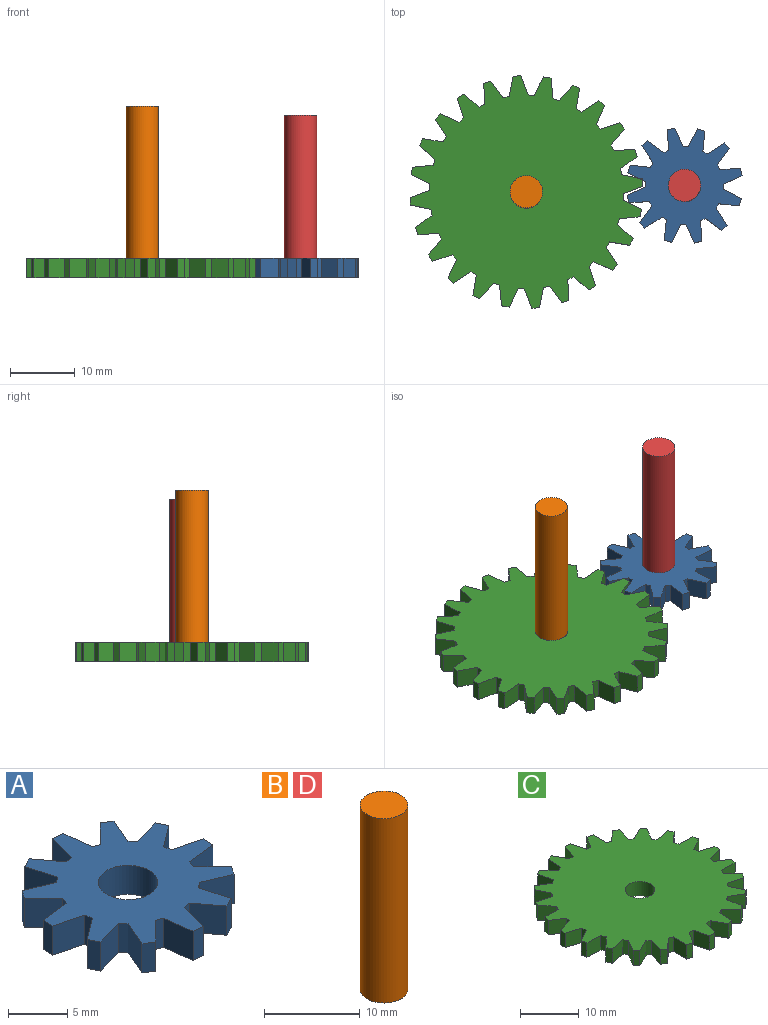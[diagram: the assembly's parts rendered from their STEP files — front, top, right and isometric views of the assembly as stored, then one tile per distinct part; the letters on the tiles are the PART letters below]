
ASSEMBLY  parts=4 mates=2
PART A: 51 faces, bbox 18x18x3 mm
  f0: plane 3x1.17mm, normal (-1,0.07,0), area 3.5mm2, adj f1,f48,f49,f50
  f1: plane 3.05x3mm, normal (-0.25,-0.97,0), area 9.5mm2, adj f0,f2,f49,f50
  f2: plane 3x0.77mm, normal (-0.98,-0.2,0), area 2.4mm2, adj f1,f3,f49,f50
  f3: plane 3x2.52mm, normal (-0.6,0.8,0), area 9.5mm2, adj f2,f4,f49,f50
  f4: plane 3x1.06mm, normal (-0.9,-0.44,0), area 3.5mm2, adj f3,f5,f49,f50
  f5: plane 3.03x3mm, normal (0.27,-0.96,0), area 9.5mm2, adj f4,f6,f49,f50
  f6: plane 3x0.59mm, normal (-0.75,-0.66,0), area 2.4mm2, adj f5,f7,f49,f50
  f7: plane 3x2.9mm, normal (-0.92,0.39,0), area 9.5mm2, adj f6,f8,f49,f50
  f8: plane 3x0.98mm, normal (-0.56,-0.83,0), area 3.5mm2, adj f7,f9,f49,f50
  f9: plane 3x2.25mm, normal (0.71,-0.7,0), area 9.5mm2, adj f8,f10,f49,f50
  f10: plane 3x0.74mm, normal (-0.32,-0.95,0), area 2.4mm2, adj f9,f11,f49,f50
  f11: plane 3.13x3mm, normal (-0.99,-0.12,0), area 9.5mm2, adj f10,f12,f49,f50
  f12: plane 3x1.17mm, normal (-0.07,-1,0), area 3.5mm2, adj f11,f13,f49,f50
  f13: plane 3.05x3mm, normal (0.97,-0.25,0), area 9.5mm2, adj f12,f14,f49,f50
  f14: plane 3x0.77mm, normal (0.2,-0.98,0), area 2.4mm2, adj f13,f15,f49,f50
  f15: plane 3x2.52mm, normal (-0.8,-0.6,0), area 9.5mm2, adj f14,f16,f49,f50
  f16: plane 3x1.06mm, normal (0.44,-0.9,0), area 3.5mm2, adj f15,f17,f49,f50
  f17: plane 3.03x3mm, normal (0.96,0.27,0), area 9.5mm2, adj f16,f18,f49,f50
  f18: plane 3x0.59mm, normal (0.66,-0.75,0), area 2.4mm2, adj f17,f19,f49,f50
  f19: plane 3x2.9mm, normal (-0.39,-0.92,0), area 9.5mm2, adj f18,f20,f49,f50
  f20: plane 3x0.98mm, normal (0.83,-0.56,0), area 3.5mm2, adj f19,f21,f49,f50
  f21: plane 3x2.25mm, normal (0.7,0.71,0), area 9.5mm2, adj f20,f22,f49,f50
  f22: plane 3x0.74mm, normal (0.95,-0.32,0), area 2.4mm2, adj f21,f23,f49,f50
  f23: plane 3.13x3mm, normal (0.12,-0.99,0), area 9.5mm2, adj f22,f24,f49,f50
  f24: plane 3x1.17mm, normal (1,-0.07,0), area 3.5mm2, adj f23,f25,f49,f50
  f25: plane 3.05x3mm, normal (0.25,0.97,0), area 9.5mm2, adj f24,f26,f49,f50
  f26: plane 3x0.77mm, normal (0.98,0.2,0), area 2.4mm2, adj f25,f27,f49,f50
  f27: plane 3x2.52mm, normal (0.6,-0.8,0), area 9.5mm2, adj f26,f28,f49,f50
  f28: plane 3x1.06mm, normal (0.9,0.44,0), area 3.5mm2, adj f27,f29,f49,f50
  f29: plane 3.03x3mm, normal (-0.27,0.96,0), area 9.5mm2, adj f28,f30,f49,f50
  f30: plane 3x0.59mm, normal (0.75,0.66,0), area 2.4mm2, adj f29,f31,f49,f50
  f31: plane 3x2.9mm, normal (0.92,-0.39,0), area 9.5mm2, adj f30,f32,f49,f50
  f32: plane 3x0.98mm, normal (0.56,0.83,0), area 3.5mm2, adj f31,f33,f49,f50
  f33: plane 3x2.25mm, normal (-0.71,0.7,0), area 9.5mm2, adj f32,f34,f49,f50
  f34: plane 3x0.74mm, normal (0.32,0.95,0), area 2.4mm2, adj f33,f35,f49,f50
  f35: plane 3.13x3mm, normal (0.99,0.12,0), area 9.5mm2, adj f34,f36,f49,f50
  f36: plane 3x1.17mm, normal (0.07,1,0), area 3.5mm2, adj f35,f37,f49,f50
  f37: plane 3.05x3mm, normal (-0.97,0.25,0), area 9.5mm2, adj f36,f38,f49,f50
  f38: plane 3x0.77mm, normal (-0.2,0.98,0), area 2.4mm2, adj f37,f39,f49,f50
  f39: plane 3x2.52mm, normal (0.8,0.6,0), area 9.5mm2, adj f38,f40,f49,f50
  f40: plane 3x1.06mm, normal (-0.44,0.9,0), area 3.5mm2, adj f39,f41,f49,f50
  f41: plane 3.03x3mm, normal (-0.96,-0.27,0), area 9.5mm2, adj f40,f42,f49,f50
  f42: plane 3x0.59mm, normal (-0.66,0.75,0), area 2.4mm2, adj f41,f43,f49,f50
  f43: plane 3x2.9mm, normal (0.39,0.92,0), area 9.5mm2, adj f42,f44,f49,f50
  f44: plane 3x0.98mm, normal (-0.83,0.56,0), area 3.5mm2, adj f43,f45,f49,f50
  f45: plane 3x2.25mm, normal (-0.7,-0.71,0), area 9.5mm2, adj f44,f46,f49,f50
  f46: plane 3x0.74mm, normal (-0.95,0.32,0), area 2.4mm2, adj f45,f48,f49,f50
  f47: cylinder r=2.5mm len=5mm, axis (0,0,-1), area 47.1mm2, adj f49,f50
  f48: plane 3.13x3mm, normal (-0.12,0.99,0), area 9.5mm2, adj f0,f46,f49,f50
  f49: plane 18x18mm, normal (0,0,1), area 156.6mm2, adj f0,f1,f2,f3,f4,f5,f6,f7
  f50: plane 18x18mm, normal (0,0,-1), area 156.6mm2, adj f0,f1,f2,f3,f4,f5,f6,f7
PART B: 3 faces, bbox 5x5x23.5 mm
  f0: cylinder r=2.5mm len=23.54mm, axis (0,0,-1), area 369.8mm2, adj f1,f2
  f1: plane 5x5mm, normal (0,0,1), area 19.6mm2, adj f0
  f2: plane 5x5mm, normal (0,0,-1), area 19.6mm2, adj f0
PART C: 99 faces, bbox 36x36x3 mm
  f0: plane 3x1.18mm, normal (-1,0.03,0), area 3.5mm2, adj f1,f96,f97,f98
  f1: plane 3.03x3mm, normal (-0.31,-0.95,0), area 9.6mm2, adj f0,f2,f97,f98
  f2: plane 3x0.98mm, normal (-1,-0.1,0), area 2.9mm2, adj f1,f3,f97,f98
  f3: plane 3x2.78mm, normal (-0.49,0.87,0), area 9.6mm2, adj f2,f4,f97,f98
  f4: plane 3x1.15mm, normal (-0.97,-0.23,0), area 3.5mm2, adj f3,f5,f97,f98
  f5: plane 3.18x3mm, normal (-0.05,-1,0), area 9.6mm2, adj f4,f6,f97,f98
  f6: plane 3x0.92mm, normal (-0.94,-0.35,0), area 2.9mm2, adj f5,f7,f97,f98
  f7: plane 3x2.29mm, normal (-0.7,0.72,0), area 9.6mm2, adj f6,f8,f97,f98
  f8: plane 3x1.04mm, normal (-0.88,-0.47,0), area 3.5mm2, adj f7,f9,f97,f98
  f9: plane 3.12x3mm, normal (0.21,-0.98,0), area 9.6mm2, adj f8,f10,f97,f98
  f10: plane 3x0.8mm, normal (-0.81,-0.58,0), area 2.9mm2, adj f9,f11,f97,f98
  f11: plane 3x2.74mm, normal (-0.86,0.51,0), area 9.6mm2, adj f10,f12,f97,f98
  f12: plane 3x0.86mm, normal (-0.73,-0.68,0), area 3.5mm2, adj f11,f13,f97,f98
  f13: plane 3x2.84mm, normal (0.46,-0.89,0), area 9.6mm2, adj f12,f14,f97,f98
  f14: plane 3x0.76mm, normal (-0.63,-0.77,0), area 2.9mm2, adj f13,f15,f97,f98
  f15: plane 3.07x3mm, normal (-0.96,0.27,0), area 9.6mm2, adj f14,f16,f97,f98
  f16: plane 3x1mm, normal (-0.53,-0.85,0), area 3.5mm2, adj f15,f17,f97,f98
  f17: plane 3x2.37mm, normal (0.67,-0.74,0), area 9.6mm2, adj f16,f18,f97,f98
  f18: plane 3x0.89mm, normal (-0.41,-0.91,0), area 2.9mm2, adj f17,f19,f97,f98
  f19: plane 3.19x3mm, normal (-1,0.01,0), area 9.6mm2, adj f18,f20,f97,f98
  f20: plane 3x1.13mm, normal (-0.29,-0.96,0), area 3.5mm2, adj f19,f21,f97,f98
  f21: plane 3x2.68mm, normal (0.84,-0.54,0), area 9.6mm2, adj f20,f22,f97,f98
  f22: plane 3x0.97mm, normal (-0.16,-0.99,0), area 2.9mm2, adj f21,f23,f97,f98
  f23: plane 3.09x3mm, normal (-0.97,-0.24,0), area 9.6mm2, adj f22,f24,f97,f98
  f24: plane 3x1.18mm, normal (-0.03,-1,0), area 3.5mm2, adj f23,f25,f97,f98
  f25: plane 3.03x3mm, normal (0.95,-0.31,0), area 9.6mm2, adj f24,f26,f97,f98
  f26: plane 3x0.98mm, normal (0.1,-1,0), area 2.9mm2, adj f25,f27,f97,f98
  f27: plane 3x2.78mm, normal (-0.87,-0.49,0), area 9.6mm2, adj f26,f28,f97,f98
  f28: plane 3x1.15mm, normal (0.23,-0.97,0), area 3.5mm2, adj f27,f29,f97,f98
  f29: plane 3.18x3mm, normal (1,-0.05,0), area 9.6mm2, adj f28,f30,f97,f98
  f30: plane 3x0.92mm, normal (0.35,-0.94,0), area 2.9mm2, adj f29,f31,f97,f98
  f31: plane 3x2.29mm, normal (-0.72,-0.7,0), area 9.6mm2, adj f30,f32,f97,f98
  f32: plane 3x1.04mm, normal (0.47,-0.88,0), area 3.5mm2, adj f31,f33,f97,f98
  f33: plane 3.12x3mm, normal (0.98,0.21,0), area 9.6mm2, adj f32,f34,f97,f98
  f34: plane 3x0.8mm, normal (0.58,-0.81,0), area 2.9mm2, adj f33,f35,f97,f98
  f35: plane 3x2.74mm, normal (-0.51,-0.86,0), area 9.6mm2, adj f34,f36,f97,f98
  f36: plane 3x0.86mm, normal (0.68,-0.73,0), area 3.5mm2, adj f35,f37,f97,f98
  f37: plane 3x2.84mm, normal (0.89,0.46,0), area 9.6mm2, adj f36,f38,f97,f98
  f38: plane 3x0.76mm, normal (0.77,-0.63,0), area 2.9mm2, adj f37,f39,f97,f98
  f39: plane 3.07x3mm, normal (-0.27,-0.96,0), area 9.6mm2, adj f38,f40,f97,f98
  f40: plane 3x1mm, normal (0.85,-0.53,0), area 3.5mm2, adj f39,f41,f97,f98
  f41: plane 3x2.37mm, normal (0.74,0.67,0), area 9.6mm2, adj f40,f42,f97,f98
  f42: plane 3x0.89mm, normal (0.91,-0.41,0), area 2.9mm2, adj f41,f43,f97,f98
  f43: plane 3.19x3mm, normal (-0.01,-1,0), area 9.6mm2, adj f42,f44,f97,f98
  f44: plane 3x1.13mm, normal (0.96,-0.29,0), area 3.5mm2, adj f43,f45,f97,f98
  f45: plane 3x2.68mm, normal (0.54,0.84,0), area 9.6mm2, adj f44,f46,f97,f98
  f46: plane 3x0.97mm, normal (0.99,-0.16,0), area 2.9mm2, adj f45,f47,f97,f98
  f47: plane 3.09x3mm, normal (0.24,-0.97,0), area 9.6mm2, adj f46,f48,f97,f98
  f48: plane 3x1.18mm, normal (1,-0.03,0), area 3.5mm2, adj f47,f49,f97,f98
  f49: plane 3.03x3mm, normal (0.31,0.95,0), area 9.6mm2, adj f48,f50,f97,f98
  f50: plane 3x0.98mm, normal (1,0.1,0), area 2.9mm2, adj f49,f51,f97,f98
  f51: plane 3x2.78mm, normal (0.49,-0.87,0), area 9.6mm2, adj f50,f52,f97,f98
  f52: plane 3x1.15mm, normal (0.97,0.23,0), area 3.5mm2, adj f51,f53,f97,f98
  f53: plane 3.18x3mm, normal (0.05,1,0), area 9.6mm2, adj f52,f54,f97,f98
  f54: plane 3x0.92mm, normal (0.94,0.35,0), area 2.9mm2, adj f53,f55,f97,f98
  f55: plane 3x2.29mm, normal (0.7,-0.72,0), area 9.6mm2, adj f54,f56,f97,f98
  f56: plane 3x1.04mm, normal (0.88,0.47,0), area 3.5mm2, adj f55,f57,f97,f98
  f57: plane 3.12x3mm, normal (-0.21,0.98,0), area 9.6mm2, adj f56,f58,f97,f98
  f58: plane 3x0.8mm, normal (0.81,0.58,0), area 2.9mm2, adj f57,f59,f97,f98
  f59: plane 3x2.74mm, normal (0.86,-0.51,0), area 9.6mm2, adj f58,f60,f97,f98
  f60: plane 3x0.86mm, normal (0.73,0.68,0), area 3.5mm2, adj f59,f61,f97,f98
  f61: plane 3x2.84mm, normal (-0.46,0.89,0), area 9.6mm2, adj f60,f62,f97,f98
  f62: plane 3x0.76mm, normal (0.63,0.77,0), area 2.9mm2, adj f61,f63,f97,f98
  f63: plane 3.07x3mm, normal (0.96,-0.27,0), area 9.6mm2, adj f62,f64,f97,f98
  f64: plane 3x1mm, normal (0.53,0.85,0), area 3.5mm2, adj f63,f65,f97,f98
  f65: plane 3x2.37mm, normal (-0.67,0.74,0), area 9.6mm2, adj f64,f66,f97,f98
  f66: plane 3x0.89mm, normal (0.41,0.91,0), area 2.9mm2, adj f65,f67,f97,f98
  f67: plane 3.19x3mm, normal (1,-0.01,0), area 9.6mm2, adj f66,f68,f97,f98
  f68: plane 3x1.13mm, normal (0.29,0.96,0), area 3.5mm2, adj f67,f69,f97,f98
  f69: plane 3x2.68mm, normal (-0.84,0.54,0), area 9.6mm2, adj f68,f70,f97,f98
  f70: plane 3x0.97mm, normal (0.16,0.99,0), area 2.9mm2, adj f69,f71,f97,f98
  f71: plane 3.09x3mm, normal (0.97,0.24,0), area 9.6mm2, adj f70,f72,f97,f98
  f72: plane 3x1.18mm, normal (0.03,1,0), area 3.5mm2, adj f71,f73,f97,f98
  f73: plane 3.03x3mm, normal (-0.95,0.31,0), area 9.6mm2, adj f72,f74,f97,f98
  f74: plane 3x0.98mm, normal (-0.1,1,0), area 2.9mm2, adj f73,f75,f97,f98
  f75: plane 3x2.78mm, normal (0.87,0.49,0), area 9.6mm2, adj f74,f76,f97,f98
  f76: plane 3x1.15mm, normal (-0.23,0.97,0), area 3.5mm2, adj f75,f77,f97,f98
  f77: plane 3.18x3mm, normal (-1,0.05,0), area 9.6mm2, adj f76,f78,f97,f98
  f78: plane 3x0.92mm, normal (-0.35,0.94,0), area 2.9mm2, adj f77,f79,f97,f98
  f79: plane 3x2.29mm, normal (0.72,0.7,0), area 9.6mm2, adj f78,f80,f97,f98
  f80: plane 3x1.04mm, normal (-0.47,0.88,0), area 3.5mm2, adj f79,f81,f97,f98
  f81: plane 3.12x3mm, normal (-0.98,-0.21,0), area 9.6mm2, adj f80,f82,f97,f98
  f82: plane 3x0.8mm, normal (-0.58,0.81,0), area 2.9mm2, adj f81,f83,f97,f98
  f83: plane 3x2.74mm, normal (0.51,0.86,0), area 9.6mm2, adj f82,f84,f97,f98
  f84: plane 3x0.86mm, normal (-0.68,0.73,0), area 3.5mm2, adj f83,f85,f97,f98
  f85: plane 3x2.84mm, normal (-0.89,-0.46,0), area 9.6mm2, adj f84,f86,f97,f98
  f86: plane 3x0.76mm, normal (-0.77,0.63,0), area 2.9mm2, adj f85,f87,f97,f98
  f87: plane 3.07x3mm, normal (0.27,0.96,0), area 9.6mm2, adj f86,f88,f97,f98
  f88: plane 3x1mm, normal (-0.85,0.53,0), area 3.5mm2, adj f87,f89,f97,f98
  f89: plane 3x2.37mm, normal (-0.74,-0.67,0), area 9.6mm2, adj f88,f90,f97,f98
  f90: plane 3x0.89mm, normal (-0.91,0.41,0), area 2.9mm2, adj f89,f91,f97,f98
  f91: plane 3.19x3mm, normal (0.01,1,0), area 9.6mm2, adj f90,f92,f97,f98
  f92: plane 3x1.13mm, normal (-0.96,0.29,0), area 3.5mm2, adj f91,f93,f97,f98
  f93: plane 3x2.68mm, normal (-0.54,-0.84,0), area 9.6mm2, adj f92,f94,f97,f98
  f94: plane 3x0.97mm, normal (-0.99,0.16,0), area 2.9mm2, adj f93,f96,f97,f98
  f95: cylinder r=2.5mm len=5mm, axis (0,0,-1), area 47.1mm2, adj f97,f98
  f96: plane 3.09x3mm, normal (-0.24,0.97,0), area 9.6mm2, adj f0,f94,f97,f98
  f97: plane 36x36mm, normal (0,0,1), area 835.1mm2, adj f0,f1,f2,f3,f4,f5,f6,f7
  f98: plane 36x36mm, normal (0,0,-1), area 835.1mm2, adj f0,f1,f2,f3,f4,f5,f6,f7
PART D: same geometry as B
PLACE A rot(axis=(0,0,1),47deg) t=(14.21,-30.36,0.07)mm
PLACE B t=(45.09,0,3)mm fixed
PLACE C rot(axis=(0,0,1),156.5deg) t=(18.97,0,0)mm
PLACE D t=(69.55,0.99,1.57)mm fixed
MATE revolute D.f0 <-> A.f47  axis (0,0,-1) through (43.43,0.99,1.57)mm
MATE revolute B.f0 <-> C.f95  axis (0,0,-1) through (18.97,0,3)mm
